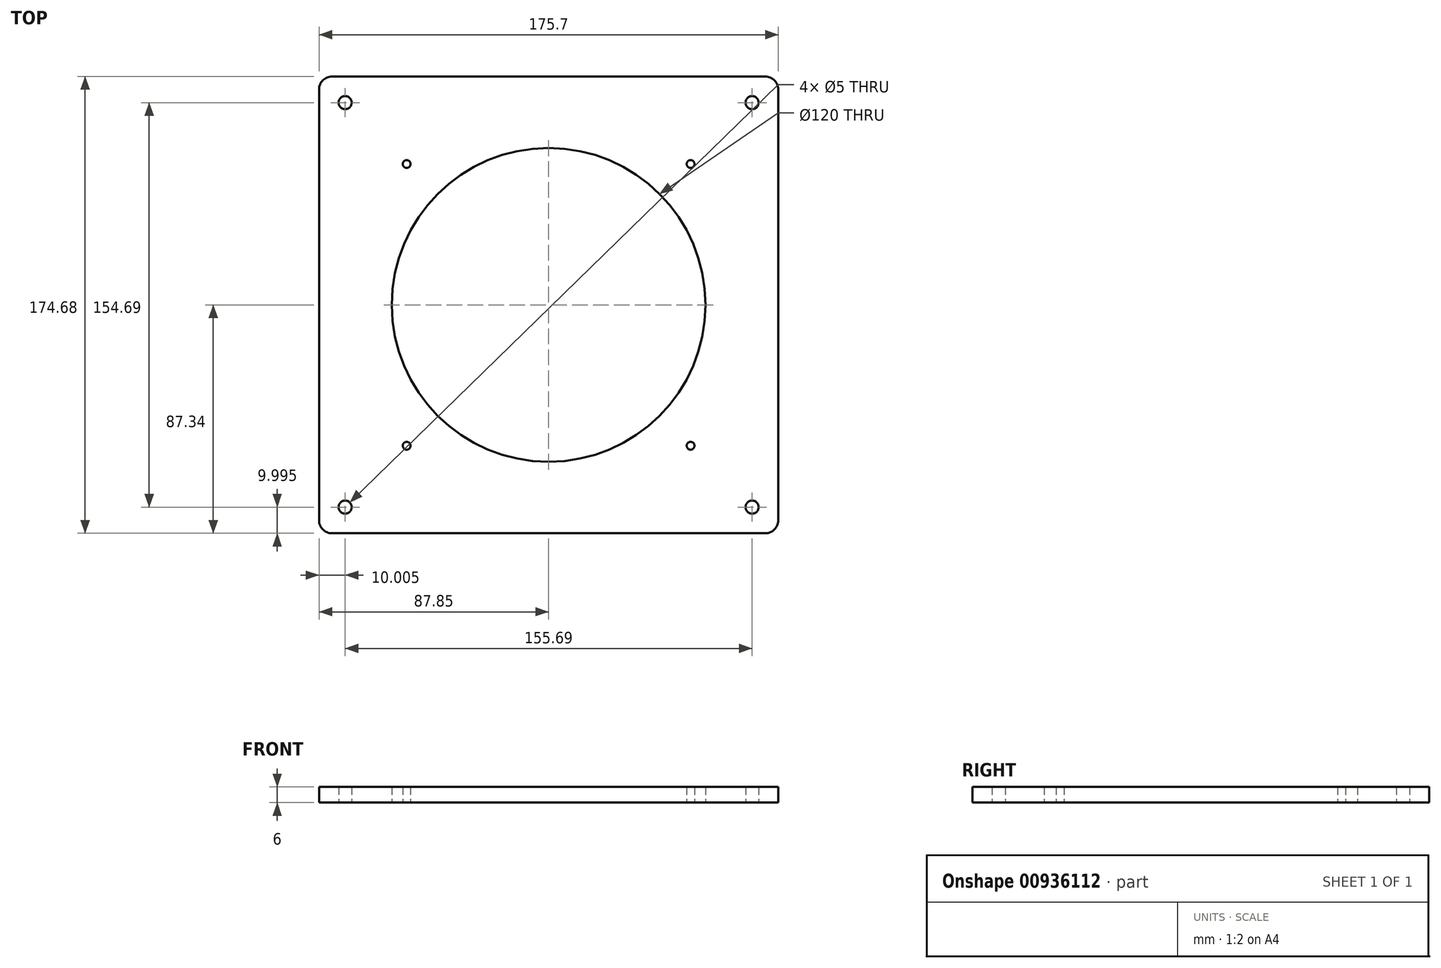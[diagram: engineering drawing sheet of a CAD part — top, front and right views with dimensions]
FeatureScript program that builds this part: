
annotation { "Feature Type Name" : "Feature", "Feature Type Description" : "" }
export const myFeature = defineFeature(function(context is Context, id is Id, definition is map)
    precondition{}
    {
        {
            var Q0;
            Q0=qCreatedBy(makeId("Top.planeOp"),FACE);
            var sketch = newSketch(context, id + "F0", { "sketchPlane" : qUnion([Q0])});
            skCircle(sketch, "E0", {"center": v(0, 0) * mm, "radius": 60 * mm});
            skLineSegment(sketch, "E1", {"start": v(-62.85, -62.35) * mm, "end": v(62.85, 62.35) * mm, "construction": true});
            skLineSegment(sketch, "E2", {"start": v(-62.84, 62.34) * mm, "end": v(62.84, -62.34) * mm, "construction": true});
            skCircle(sketch, "E3", {"center": v(-54.3, -53.88) * mm, "radius": 1.5 * mm});
            skCircle(sketch, "E4", {"center": v(54.3, 53.88) * mm, "radius": 1.5 * mm});
            skCircle(sketch, "E5", {"center": v(-54.3, 53.88) * mm, "radius": 1.5 * mm});
            skCircle(sketch, "E6", {"center": v(54.3, -53.88) * mm, "radius": 1.5 * mm});
            skLineSegment(sketch, "E7.0", {"start": v(-82.84, 87.35) * mm, "end": v(82.85, 87.34) * mm});
            skLineSegment(sketch, "E7.1", {"start": v(-87.84, 82.35) * mm, "end": v(-87.85, -82.34) * mm});
            skLineSegment(sketch, "E7.2", {"start": v(-82.85, -87.34) * mm, "end": v(82.84, -87.35) * mm});
            skLineSegment(sketch, "E7.3", {"start": v(87.85, 82.34) * mm, "end": v(87.84, -82.35) * mm});
            skPoint(sketch, "E8.visualSharp", {"position": v(-87.84, 87.35) * mm});
            skArc(sketch, "E8.filletArc", {"start": v(-82.84, 87.35) * mm, "mid": v(-86.38, 85.88) * mm, "end": v(-87.84, 82.35) * mm});
            skPoint(sketch, "E9.visualSharp", {"position": v(87.84, 87.34) * mm});
            skArc(sketch, "E9.filletArc", {"start": v(87.85, 82.34) * mm, "mid": v(86.38, 85.88) * mm, "end": v(82.85, 87.34) * mm});
            skPoint(sketch, "E10.visualSharp", {"position": v(-87.85, -87.35) * mm});
            skArc(sketch, "E10.filletArc", {"start": v(-87.85, -82.34) * mm, "mid": v(-86.38, -85.88) * mm, "end": v(-82.85, -87.34) * mm});
            skPoint(sketch, "E11.visualSharp", {"position": v(87.84, -87.35) * mm});
            skArc(sketch, "E11.filletArc", {"start": v(82.84, -87.35) * mm, "mid": v(86.38, -85.88) * mm, "end": v(87.84, -82.35) * mm});
            skCircle(sketch, "E12", {"center": v(-77.84, 77.35) * mm, "radius": 2.5 * mm});
            skCircle(sketch, "E13", {"center": v(77.85, 77.35) * mm, "radius": 2.5 * mm});
            skCircle(sketch, "E14", {"center": v(77.85, -77.35) * mm, "radius": 2.5 * mm});
            skCircle(sketch, "E15", {"center": v(-77.84, -77.35) * mm, "radius": 2.5 * mm});
            skSolve(sketch);
        }
        {
            var Q0;
            Q0 = qSketchRegion(id + "F0", true);
            extrude(context, id + "F1", {"entities" : qUnion([Q0]), "depth" : 6 * mm, "offsetDistance" : 25 * mm});
        }
    });
